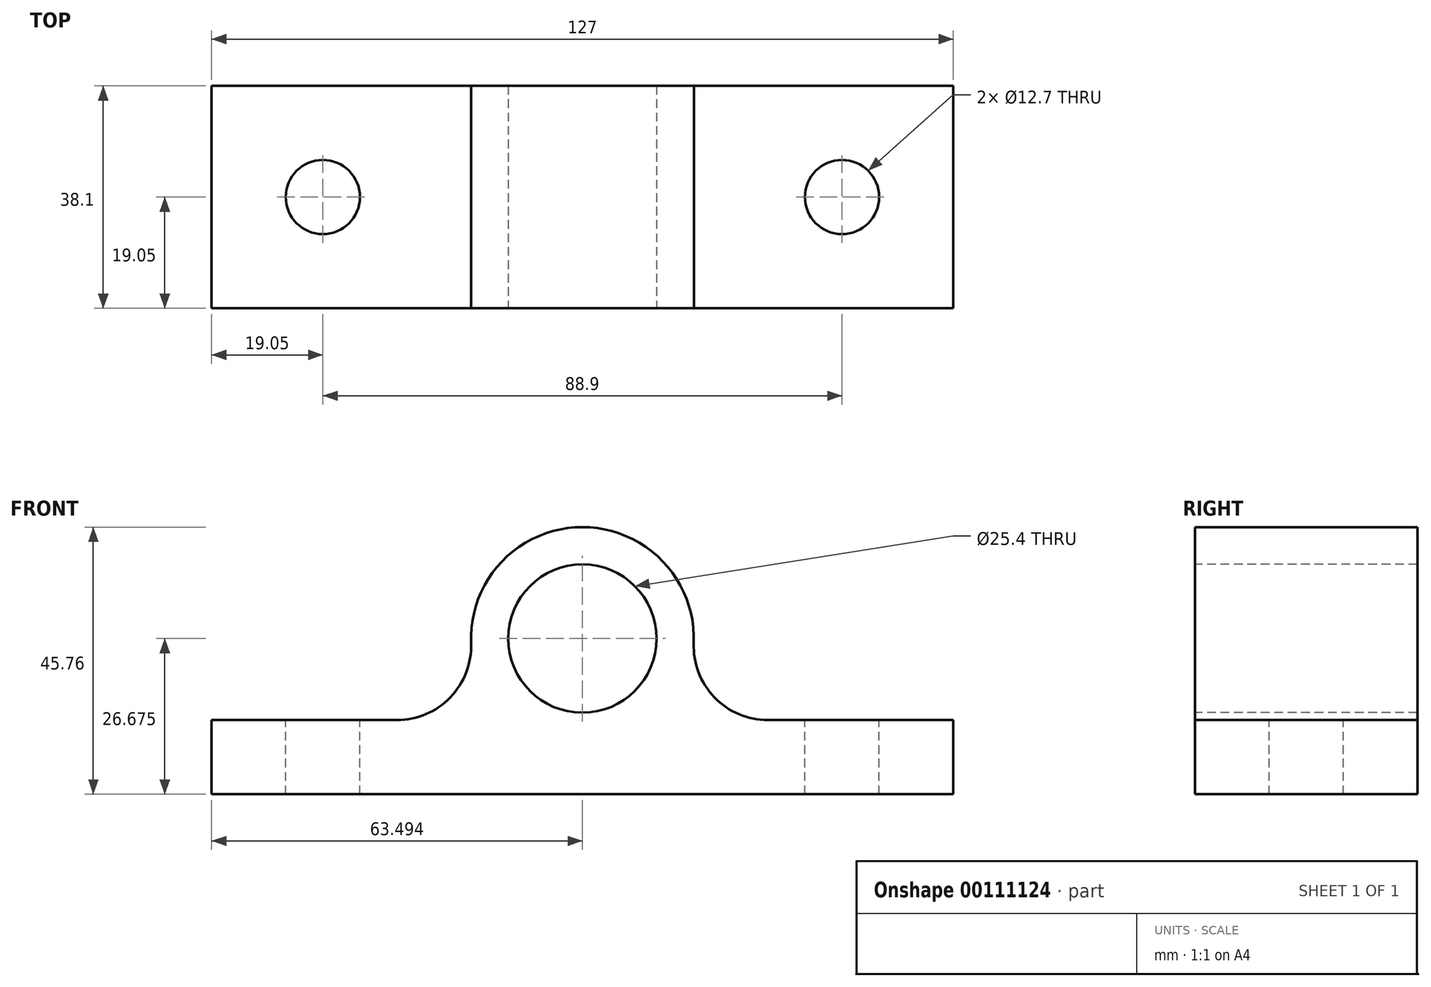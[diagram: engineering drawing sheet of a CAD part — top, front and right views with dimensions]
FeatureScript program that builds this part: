
annotation { "Feature Type Name" : "Feature", "Feature Type Description" : "" }
export const myFeature = defineFeature(function(context is Context, id is Id, definition is map)
    precondition{}
    {
        {
            var Q0;
            Q0=qCreatedBy(makeId("Front.planeOp"),FACE);
            var sketch = newSketch(context, id + "F0", { "sketchPlane" : qUnion([Q0])});
            skLineSegment(sketch, "E0", {"start": v(0, 0) * mm, "end": v(-127, 0) * mm});
            skLineSegment(sketch, "E1", {"start": v(-127, 0) * mm, "end": v(-127, 12.7) * mm});
            skLineSegment(sketch, "E2", {"start": v(-127, 12.7) * mm, "end": v(-95.26, 12.7) * mm});
            skLineSegment(sketch, "E3", {"start": v(-31.75, 12.7) * mm, "end": v(0, 12.7) * mm});
            skLineSegment(sketch, "E4", {"start": v(0, 12.7) * mm, "end": v(0, 0) * mm});
            skPoint(sketch, "E5.visualSharp", {"position": v(-44.45, 12.7) * mm});
            skArc(sketch, "E5.filletArc", {"start": v(-44.44, 25.9) * mm, "mid": v(-40.9, 16.6) * mm, "end": v(-31.75, 12.7) * mm});
            skPoint(sketch, "E6.visualSharp", {"position": v(-82.55, 12.7) * mm});
            skArc(sketch, "E6.filletArc", {"start": v(-95.26, 12.7) * mm, "mid": v(-86.1, 16.6) * mm, "end": v(-82.57, 25.9) * mm});
            skArc(sketch, "E7", {"start": v(-44.44, 25.9) * mm, "mid": v(-63.5, 45.76) * mm, "end": v(-82.57, 25.9) * mm});
            skCircle(sketch, "E8", {"center": v(-63.5, 26.68) * mm, "radius": 12.7 * mm});
            skSolve(sketch);
        }
        {
            var Q0;
            Q0=makeQuery(id+"F0.imprint","IMPRINT",FACE,{"disambiguationData":[TD([[makeQuery(id+"F0.imprint","IMPRINT",EDGE,{"derivedFrom":sQuery(id+"F0.wireOp",EDGE,"E0")}),-1.0]])]});
            extrude(context, id + "F1", {"entities" : qUnion([Q0]), "oppositeDirection" : true, "depth" : 38.1 * mm});
        }
        {
            var Q0;
            Q0=makeQuery(id+"F1.opExtrude","SWEPT_FACE",FACE,{"disambiguationData":[OSD([sQuery(id+"F0.wireOp",EDGE,"E3")])]});
            var sketch = newSketch(context, id + "F2", { "sketchPlane" : qUnion([Q0])});
            skCircle(sketch, "E9", {"center": v(-19.05, 19.05) * mm, "radius": 6.35 * mm});
            skSolve(sketch);
        }
        {
            var Q0;
            Q0=makeQuery(id+"F1.opExtrude","SWEPT_FACE",FACE,{"disambiguationData":[OSD([sQuery(id+"F0.wireOp",EDGE,"E2")])]});
            var sketch = newSketch(context, id + "F3", { "sketchPlane" : qUnion([Q0])});
            skCircle(sketch, "E10", {"center": v(-107.95, 19.05) * mm, "radius": 6.35 * mm});
            skSolve(sketch);
        }
        {
            var Q0;
            Q0=makeQuery(id+"F2.imprint","IMPRINT",FACE,{"disambiguationData":[TD([[makeQuery(id+"F2.imprint","IMPRINT",EDGE,{"derivedFrom":sQuery(id+"F2.wireOp",EDGE,"E9")}),1.0]])]});
            var Q1;
            Q1=makeQuery(id+"F3.imprint","IMPRINT",FACE,{"disambiguationData":[TD([[makeQuery(id+"F3.imprint","IMPRINT",EDGE,{"derivedFrom":sQuery(id+"F3.wireOp",EDGE,"E10")}),1.0]])]});
            extrude(context, id + "F4", {"entities" : qUnion([Q0, Q1]), "operationType" : NewBodyOperationType.REMOVE, "oppositeDirection" : true, "depth" : 12.7 * mm});
        }
    });
